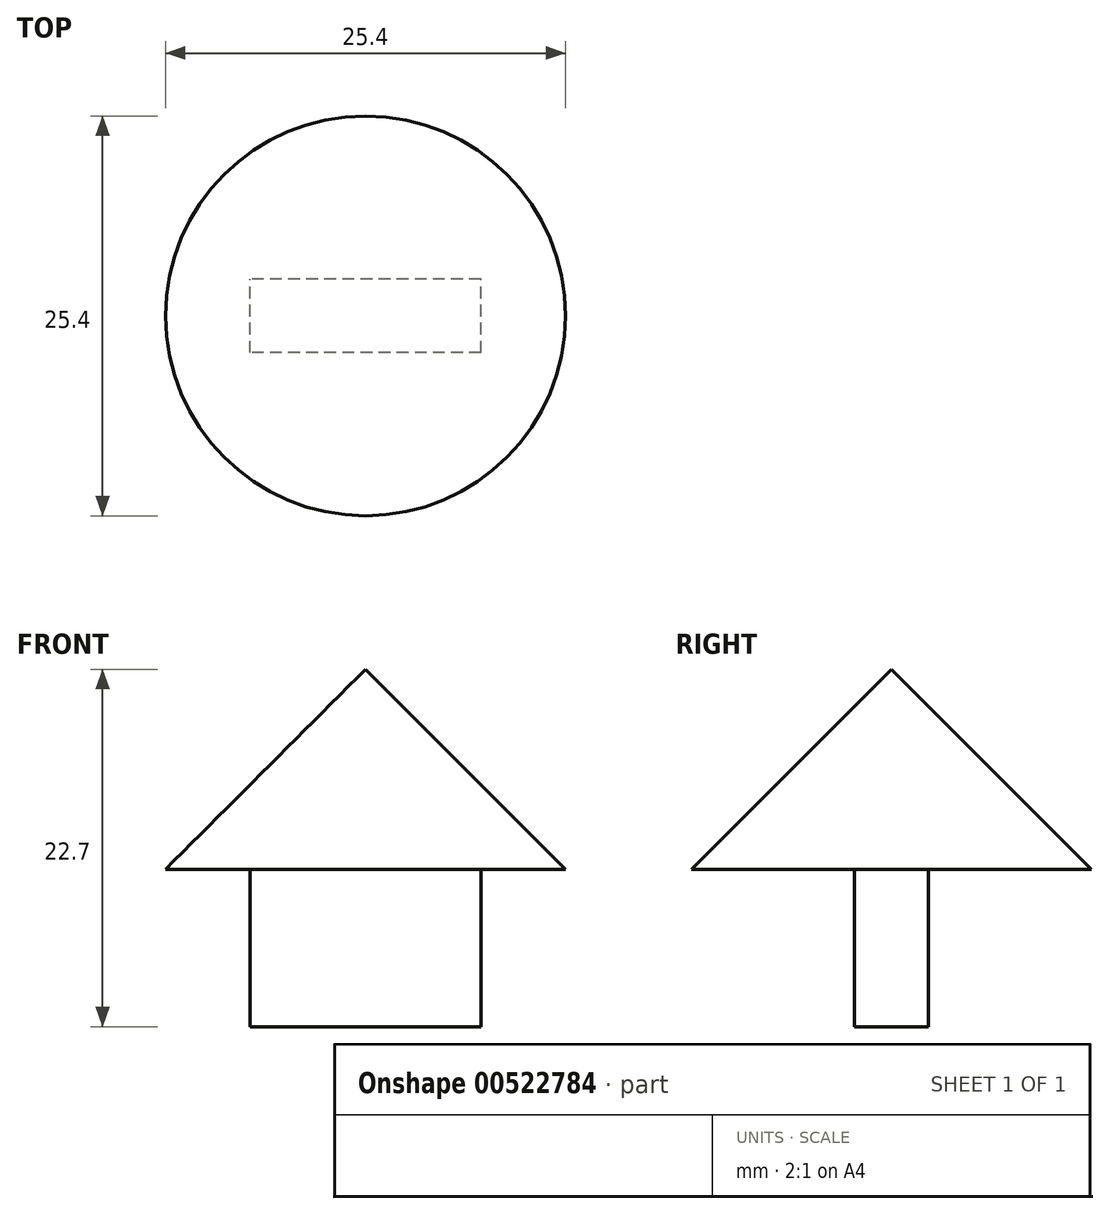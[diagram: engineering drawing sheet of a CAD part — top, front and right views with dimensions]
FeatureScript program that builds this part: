
annotation { "Feature Type Name" : "Feature", "Feature Type Description" : "" }
export const myFeature = defineFeature(function(context is Context, id is Id, definition is map)
    precondition{}
    {
        {
            var Q0;
            Q0=qCreatedBy(makeId("Front.planeOp"),FACE);
            var sketch = newSketch(context, id + "F0", { "sketchPlane" : qUnion([Q0])});
            skLineSegment(sketch, "E0", {"start": v(0, 0) * mm, "end": v(0, 12.7) * mm});
            skLineSegment(sketch, "E1", {"start": v(0, 12.7) * mm, "end": v(12.7, 0) * mm});
            skLineSegment(sketch, "E2", {"start": v(0, 0) * mm, "end": v(12.7, 0) * mm});
            skSolve(sketch);
        }
        {
            var Q0;
            Q0=qCreatedBy(makeId("Front.planeOp"),FACE);
            var sketch = newSketch(context, id + "F1", { "sketchPlane" : qUnion([Q0])});
            skLineSegment(sketch, "E3", {"start": v(0, 0) * mm, "end": v(0, 39.86) * mm});
            skSolve(sketch);
        }
        {
            var Q0;
            Q0=qSketchRegion(id+"F0",true);
            var Q1;
            Q1=sQuery(id+"F1.wireOp",EDGE,"E3");
            revolve(context, id + "F2", {"entities" : qUnion([Q0]), "axis" : qUnion([Q1]), "revolveType" : RevolveType.FULL});
        }
        {
            var Q0;
            Q0=qCreatedBy(makeId("Top.planeOp"),FACE);
            var sketch = newSketch(context, id + "F3", { "sketchPlane" : qUnion([Q0])});
            skLineSegment(sketch, "E4.rect.bottom", {"start": v(7.33, -2.34) * mm, "end": v(-7.33, -2.34) * mm});
            skLineSegment(sketch, "E4.rect.top", {"start": v(7.33, 2.34) * mm, "end": v(-7.33, 2.34) * mm});
            skLineSegment(sketch, "E4.rect.left", {"start": v(7.33, -2.34) * mm, "end": v(7.33, 2.34) * mm});
            skLineSegment(sketch, "E4.rect.right", {"start": v(-7.33, -2.34) * mm, "end": v(-7.33, 2.34) * mm});
            skPoint(sketch, "E4.rect.middle", {"position": v(0, 0) * mm});
            skSolve(sketch);
        }
        {
            var Q0;
            Q0=makeQuery(id+"F3.imprint","IMPRINT",FACE,{"disambiguationData":[TD([[makeQuery(id+"F3.imprint","IMPRINT",EDGE,{"derivedFrom":sQuery(id+"F3.wireOp",EDGE,"E4.rect.bottom")}),-1.0]])]});
            extrude(context, id + "F4", {"entities" : qUnion([Q0]), "operationType" : NewBodyOperationType.ADD, "oppositeDirection" : true, "depth" : 10 * mm});
        }
    });
